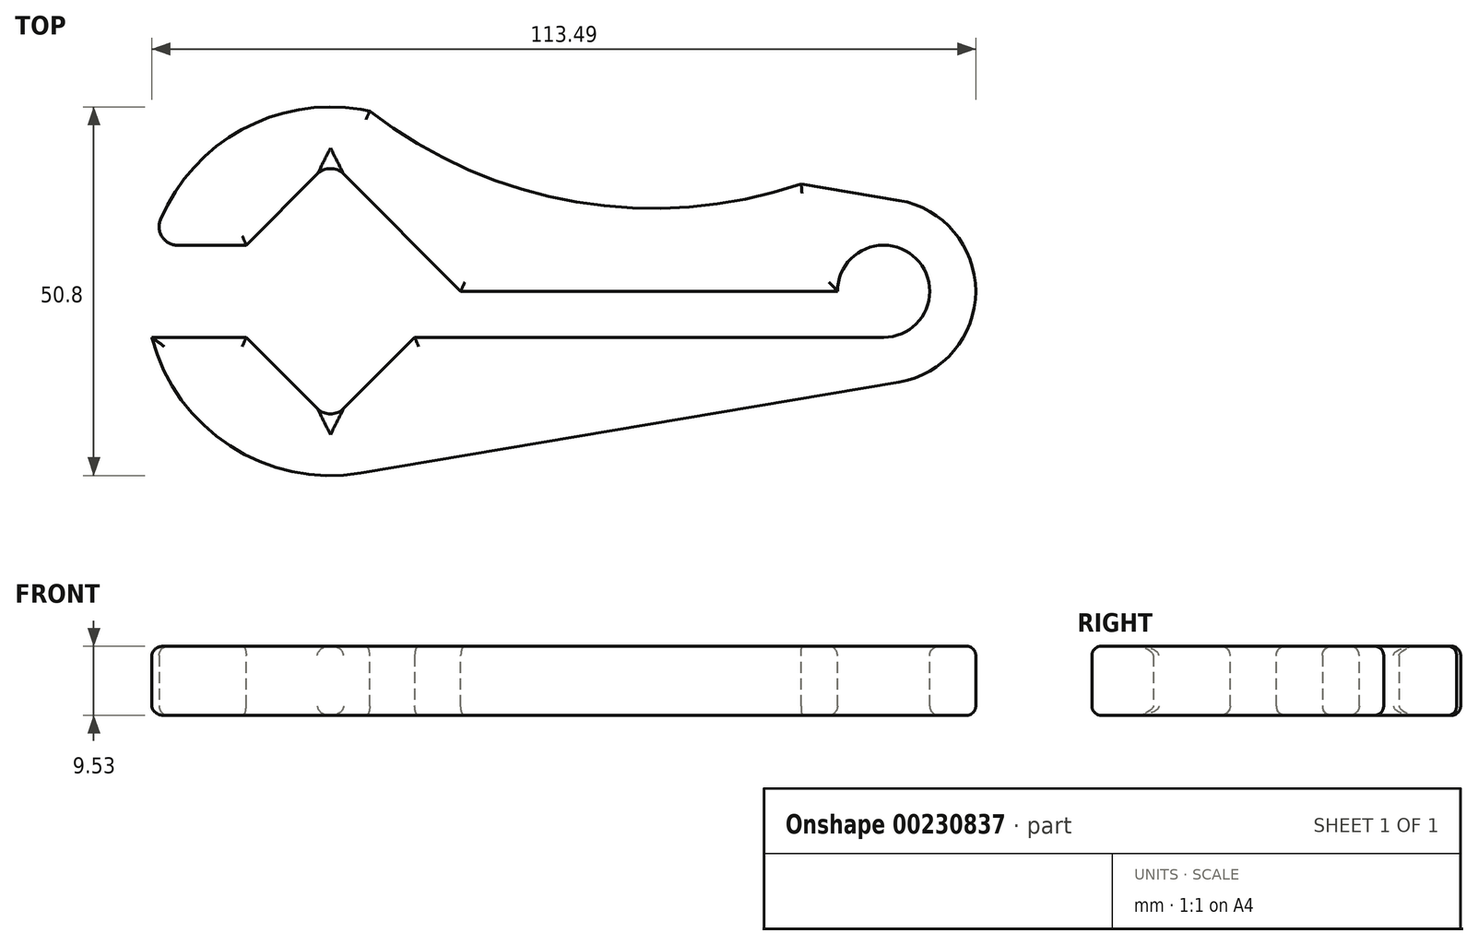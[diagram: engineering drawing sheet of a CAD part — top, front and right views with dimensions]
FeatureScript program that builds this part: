
annotation { "Feature Type Name" : "Feature", "Feature Type Description" : "" }
export const myFeature = defineFeature(function(context is Context, id is Id, definition is map)
    precondition{}
    {
        {
            var Q0;
            Q0=qCreatedBy(makeId("Top.planeOp"),FACE);
            var sketch = newSketch(context, id + "F0", { "sketchPlane" : qUnion([Q0])});
            skArc(sketch, "E0", {"start": v(4.23, 25.04) * mm, "mid": v(-25.4, 0) * mm, "end": v(4.23, -25.04) * mm});
            skArc(sketch, "E1", {"start": v(78.32, -12.52) * mm, "mid": v(88.9, 0) * mm, "end": v(78.32, 12.52) * mm});
            skLineSegment(sketch, "E2", {"start": v(4.23, 25.04) * mm, "end": v(78.32, 12.52) * mm});
            skLineSegment(sketch, "E3", {"start": v(4.23, -25.04) * mm, "end": v(78.32, -12.52) * mm});
            skPoint(sketch, "E4.orphan", {"position": v(4.23, 25.04) * mm});
            skSolve(sketch);
        }
        {
            var Q0;
            Q0=qCreatedBy(makeId("Top.planeOp"),FACE);
            var sketch = newSketch(context, id + "F1", { "sketchPlane" : qUnion([Q0])});
            skLineSegment(sketch, "E5.bottom", {"start": v(-17.96, 0) * mm, "end": v(0, 17.96) * mm});
            skLineSegment(sketch, "E5.top", {"start": v(0, -17.96) * mm, "end": v(17.96, 0) * mm});
            skLineSegment(sketch, "E5.left", {"start": v(-17.96, 0) * mm, "end": v(0, -17.96) * mm});
            skLineSegment(sketch, "E5.right", {"start": v(0, 17.96) * mm, "end": v(17.96, 0) * mm});
            skSolve(sketch);
        }
        {
            var Q0;
            Q0=qCreatedBy(makeId("Top.planeOp"),FACE);
            var sketch = newSketch(context, id + "F2", { "sketchPlane" : qUnion([Q0])});
            skArc(sketch, "E6", {"start": v(76.2, -6.35) * mm, "mid": v(80.7, 4.5) * mm, "end": v(69.85, 0) * mm});
            skLineSegment(sketch, "E7", {"start": v(76.2, -6.35) * mm, "end": v(-85.74, -6.35) * mm});
            skLineSegment(sketch, "E8", {"start": v(-85.74, 0) * mm, "end": v(-85.74, -6.35) * mm});
            skLineSegment(sketch, "E9", {"start": v(69.85, 0) * mm, "end": v(-85.74, 0) * mm});
            skPoint(sketch, "E10.orphan", {"position": v(-85.74, 6.35) * mm});
            skSolve(sketch);
        }
        {
            var Q0;
            Q0=qCreatedBy(makeId("Top.planeOp"),FACE);
            var sketch = newSketch(context, id + "F3", { "sketchPlane" : qUnion([Q0])});
            skLineSegment(sketch, "E11.bottom", {"start": v(-31.75, 6.35) * mm, "end": v(-6.35, 6.35) * mm});
            skLineSegment(sketch, "E11.top", {"start": v(-31.75, -6.35) * mm, "end": v(-6.35, -6.35) * mm});
            skLineSegment(sketch, "E11.left", {"start": v(-31.75, 6.35) * mm, "end": v(-31.75, -6.35) * mm});
            skLineSegment(sketch, "E11.right", {"start": v(-6.35, 6.35) * mm, "end": v(-6.35, -6.35) * mm});
            skSolve(sketch);
        }
        {
            var Q0;
            Q0=qCreatedBy(makeId("Top.planeOp"),FACE);
            var sketch = newSketch(context, id + "F4", { "sketchPlane" : qUnion([Q0])});
            skCircle(sketch, "E12", {"center": v(44.45, 74.93) * mm, "radius": 63.5 * mm});
            skCircle(sketch, "E13.MirrorC", {"center": v(44.45, -74.93) * mm, "radius": 63.5 * mm});
            skSolve(sketch);
        }
        {
            var Q0;
            Q0=makeQuery(id+"F0.imprint","IMPRINT",FACE,{"disambiguationData":[TD([[makeQuery(id+"F0.imprint","IMPRINT",EDGE,{"derivedFrom":sQuery(id+"F0.wireOp",EDGE,"E0")}),1.0]])]});
            extrude(context, id + "F5", {"entities" : qUnion([Q0]), "depth" : 9.52 * mm});
        }
        {
            var Q0;
            Q0=makeQuery(id+"F4.imprint","IMPRINT",FACE,{"disambiguationData":[TD([[makeQuery(id+"F4.imprint","IMPRINT",EDGE,{"derivedFrom":sQuery(id+"F4.wireOp",EDGE,"E12")}),1.0]])]});
            var Q1;
            Q1=makeQuery(id+"F4.imprint","IMPRINT",FACE,{"disambiguationData":[TD([[makeQuery(id+"F4.imprint","IMPRINT",EDGE,{"derivedFrom":sQuery(id+"F4.wireOp",EDGE,"E13.MirrorC")}),-1.0]])]});
            extrude(context, id + "F6", {"entities" : qUnion([Q0, Q1]), "operationType" : NewBodyOperationType.REMOVE, "endBound" : BoundingType.SYMMETRIC, "oppositeDirection" : true, "depth" : 25.4 * mm});
        }
        {
            var Q0;
            Q0=makeQuery(id+"F2.imprint","IMPRINT",FACE,{"disambiguationData":[TD([[makeQuery(id+"F2.imprint","IMPRINT",EDGE,{"derivedFrom":sQuery(id+"F2.wireOp",EDGE,"E6")}),1.0]])]});
            extrude(context, id + "F7", {"entities" : qUnion([Q0]), "operationType" : NewBodyOperationType.REMOVE, "endBound" : BoundingType.SYMMETRIC, "oppositeDirection" : true, "depth" : 25.4 * mm});
        }
        {
            var Q0;
            Q0=makeQuery(id+"F3.imprint","IMPRINT",FACE,{"disambiguationData":[TD([[makeQuery(id+"F3.imprint","IMPRINT",EDGE,{"derivedFrom":sQuery(id+"F3.wireOp",EDGE,"E11.bottom")}),-1.0]])]});
            extrude(context, id + "F8", {"entities" : qUnion([Q0]), "operationType" : NewBodyOperationType.REMOVE, "endBound" : BoundingType.SYMMETRIC, "depth" : 25.4 * mm});
        }
        {
            var Q0;
            Q0 = qSketchRegion(id + "F1", true);
            extrude(context, id + "F9", {"entities" : qUnion([Q0]), "operationType" : NewBodyOperationType.REMOVE, "endBound" : BoundingType.SYMMETRIC, "oppositeDirection" : true, "depth" : 25.4 * mm});
        }
        {
            var Q0;
            Q0=makeQuery(id+"F8.boolean.opBoolean","INTERSECT",EDGE,{"derivedFrom":[makeQuery(id+"F5.opExtrude","SWEPT_FACE",FACE,{"disambiguationData":[OSD([sQuery(id+"F0.wireOp",EDGE,"E0")])]}),makeQuery(id+"F8.opExtrude","SWEPT_FACE",FACE,{"disambiguationData":[OSD([sQuery(id+"F3.wireOp",EDGE,"E11.bottom")])]})]});
            var Q1;
            Q1=makeQuery(id+"F8.boolean.opBoolean","INTERSECT",EDGE,{"derivedFrom":[makeQuery(id+"F5.opExtrude","SWEPT_FACE",FACE,{"disambiguationData":[OSD([sQuery(id+"F0.wireOp",EDGE,"E0")])]}),makeQuery(id+"F8.opExtrude","SWEPT_FACE",FACE,{"disambiguationData":[OSD([sQuery(id+"F3.wireOp",EDGE,"E11.top")])]})]});
            fillet(context, id + "F10", {"entities" : qUnion([Q0, Q1]), "radius" : 2.54 * mm, "tangentPropagation" : true, "allowEdgeOverflow" : false});
        }
        {
            var Q0;
            {var subQ0=sQuery(id+"F0.wireOp",EDGE,"E0");var subQ1=sQuery(id+"F0.wireOp",EDGE,"E2");Q0=makeQuery(id+"F8.boolean.opBoolean","SPLIT",EDGE,{"disambiguationData":[TD([makeQuery(id+"F5.opExtrude","SWEPT_FACE",FACE,{"disambiguationData":[OSD([subQ1])]})])],"derivedFrom":makeQuery(id+"F5.opExtrude","CAP_EDGE",EDGE,{"disambiguationData":[OSD([subQ0])],"isStart":false})});}
            var Q1;
            Q1=makeQuery(id+"F6.boolean.opBoolean","INTERSECT",EDGE,{"derivedFrom":[makeQuery(id+"F5.opExtrude","CAP_FACE",FACE,{"disambiguationData":[OSD([sQuery(id+"F0.wireOp",EDGE,"E0"),sQuery(id+"F0.wireOp",EDGE,"E1"),sQuery(id+"F0.wireOp",EDGE,"E2"),sQuery(id+"F0.wireOp",EDGE,"E3")])],"isStart":false}),makeQuery(id+"F6.opExtrude","SWEPT_FACE",FACE,{"disambiguationData":[OSD([sQuery(id+"F4.wireOp",EDGE,"E12")])]})]});
            var Q2;
            Q2=makeQuery(id+"F9.boolean.opBoolean","INTERSECT",EDGE,{"derivedFrom":[makeQuery(id+"F5.opExtrude","CAP_FACE",FACE,{"disambiguationData":[OSD([sQuery(id+"F0.wireOp",EDGE,"E0"),sQuery(id+"F0.wireOp",EDGE,"E1"),sQuery(id+"F0.wireOp",EDGE,"E2"),sQuery(id+"F0.wireOp",EDGE,"E3")])],"isStart":false}),makeQuery(id+"F9.opExtrude","SWEPT_FACE",FACE,{"disambiguationData":[OSD([sQuery(id+"F1.wireOp",EDGE,"E5.bottom")])]})]});
            var Q3;
            Q3=makeQuery(id+"F9.boolean.opBoolean","INTERSECT",EDGE,{"derivedFrom":[makeQuery(id+"F5.opExtrude","CAP_FACE",FACE,{"disambiguationData":[OSD([sQuery(id+"F0.wireOp",EDGE,"E0"),sQuery(id+"F0.wireOp",EDGE,"E1"),sQuery(id+"F0.wireOp",EDGE,"E2"),sQuery(id+"F0.wireOp",EDGE,"E3")])],"isStart":false}),makeQuery(id+"F9.opExtrude","SWEPT_FACE",FACE,{"disambiguationData":[OSD([sQuery(id+"F1.wireOp",EDGE,"E5.right")])]})]});
            var Q4;
            Q4=makeQuery(id+"F7.boolean.opBoolean","INTERSECT",EDGE,{"derivedFrom":[makeQuery(id+"F5.opExtrude","CAP_FACE",FACE,{"disambiguationData":[OSD([sQuery(id+"F0.wireOp",EDGE,"E0"),sQuery(id+"F0.wireOp",EDGE,"E1"),sQuery(id+"F0.wireOp",EDGE,"E2"),sQuery(id+"F0.wireOp",EDGE,"E3")])],"isStart":false}),makeQuery(id+"F7.opExtrude","SWEPT_FACE",FACE,{"disambiguationData":[OSD([sQuery(id+"F2.wireOp",EDGE,"E9")])]})]});
            var Q5;
            Q5=makeQuery(id+"F9.boolean.opBoolean","INTERSECT",EDGE,{"derivedFrom":[makeQuery(id+"F5.opExtrude","CAP_FACE",FACE,{"disambiguationData":[OSD([sQuery(id+"F0.wireOp",EDGE,"E0"),sQuery(id+"F0.wireOp",EDGE,"E1"),sQuery(id+"F0.wireOp",EDGE,"E2"),sQuery(id+"F0.wireOp",EDGE,"E3")])],"isStart":false}),makeQuery(id+"F9.opExtrude","SWEPT_FACE",FACE,{"disambiguationData":[OSD([sQuery(id+"F1.wireOp",EDGE,"E5.top")])]})]});
            var Q6;
            Q6=makeQuery(id+"F9.boolean.opBoolean","INTERSECT",EDGE,{"derivedFrom":[makeQuery(id+"F5.opExtrude","CAP_FACE",FACE,{"disambiguationData":[OSD([sQuery(id+"F0.wireOp",EDGE,"E0"),sQuery(id+"F0.wireOp",EDGE,"E1"),sQuery(id+"F0.wireOp",EDGE,"E2"),sQuery(id+"F0.wireOp",EDGE,"E3")])],"isStart":false}),makeQuery(id+"F9.opExtrude","SWEPT_FACE",FACE,{"disambiguationData":[OSD([sQuery(id+"F1.wireOp",EDGE,"E5.left")])]})]});
            var Q7;
            Q7=makeQuery(id+"F8.boolean.opBoolean","INTERSECT",EDGE,{"derivedFrom":[makeQuery(id+"F5.opExtrude","CAP_FACE",FACE,{"disambiguationData":[OSD([sQuery(id+"F0.wireOp",EDGE,"E0"),sQuery(id+"F0.wireOp",EDGE,"E1"),sQuery(id+"F0.wireOp",EDGE,"E2"),sQuery(id+"F0.wireOp",EDGE,"E3")])],"isStart":false}),makeQuery(id+"F8.opExtrude","SWEPT_FACE",FACE,{"disambiguationData":[OSD([sQuery(id+"F3.wireOp",EDGE,"E11.top")])]})]});
            var Q8;
            Q8=makeQuery(id+"F7.boolean.opBoolean","INTERSECT",EDGE,{"derivedFrom":[makeQuery(id+"F5.opExtrude","CAP_FACE",FACE,{"disambiguationData":[OSD([sQuery(id+"F0.wireOp",EDGE,"E0"),sQuery(id+"F0.wireOp",EDGE,"E1"),sQuery(id+"F0.wireOp",EDGE,"E2"),sQuery(id+"F0.wireOp",EDGE,"E3")])],"isStart":false}),makeQuery(id+"F7.opExtrude","SWEPT_FACE",FACE,{"disambiguationData":[OSD([sQuery(id+"F2.wireOp",EDGE,"E7")])]})]});
            var Q9;
            Q9=makeQuery(id+"F6.boolean.opBoolean","INTERSECT",EDGE,{"derivedFrom":[makeQuery(id+"F5.opExtrude","CAP_FACE",FACE,{"disambiguationData":[OSD([sQuery(id+"F0.wireOp",EDGE,"E0"),sQuery(id+"F0.wireOp",EDGE,"E1"),sQuery(id+"F0.wireOp",EDGE,"E2"),sQuery(id+"F0.wireOp",EDGE,"E3")])],"isStart":false}),makeQuery(id+"F6.opExtrude","SWEPT_FACE",FACE,{"disambiguationData":[OSD([sQuery(id+"F4.wireOp",EDGE,"E13.MirrorC")])]})]});
            var Q10;
            {var subQ0=sQuery(id+"F0.wireOp",EDGE,"E2");var subQ1=sQuery(id+"F0.wireOp",EDGE,"E1");Q10=makeQuery(id+"F6.boolean.opBoolean","SPLIT",EDGE,{"disambiguationData":[TD([makeQuery(id+"F5.opExtrude","SWEPT_FACE",FACE,{"disambiguationData":[OSD([subQ1])]})])],"derivedFrom":makeQuery(id+"F5.opExtrude","CAP_EDGE",EDGE,{"disambiguationData":[OSD([subQ0])],"isStart":false})});}
            fillet(context, id + "F11", {"entities" : qUnion([Q0, Q1, Q2, Q3, Q4, Q5, Q6, Q7, Q8, Q9, Q10]), "radius" : 1.27 * mm, "tangentPropagation" : true, "allowEdgeOverflow" : false});
        }
        {
            var Q0;
            Q0=makeQuery(id+"F5.opExtrude","CAP_FACE",FACE,{"disambiguationData":[OSD([sQuery(id+"F0.wireOp",EDGE,"E0"),sQuery(id+"F0.wireOp",EDGE,"E1"),sQuery(id+"F0.wireOp",EDGE,"E2"),sQuery(id+"F0.wireOp",EDGE,"E3")])],"isStart":true});
            fillet(context, id + "F12", {"entities" : qUnion([Q0]), "radius" : 1.27 * mm, "tangentPropagation" : true, "allowEdgeOverflow" : false});
        }
        {
            var Q0;
            Q0=makeQuery(id+"F9.boolean.opBoolean","COPY",EDGE,{"derivedFrom":makeQuery(id+"F9.opExtrude","SWEPT_EDGE",EDGE,{"disambiguationData":[OSD([sQuery(id+"F1.wireOp",EDGE,"E5.top"),sQuery(id+"F1.wireOp",EDGE,"E5.left")])]})});
            var Q1;
            Q1=makeQuery(id+"F9.boolean.opBoolean","COPY",EDGE,{"derivedFrom":makeQuery(id+"F9.opExtrude","SWEPT_EDGE",EDGE,{"disambiguationData":[OSD([sQuery(id+"F1.wireOp",EDGE,"E5.bottom"),sQuery(id+"F1.wireOp",EDGE,"E5.right")])]})});
            fillet(context, id + "F13", {"entities" : qUnion([Q0, Q1]), "radius" : 2.54 * mm, "tangentPropagation" : true, "allowEdgeOverflow" : false});
        }
    });
